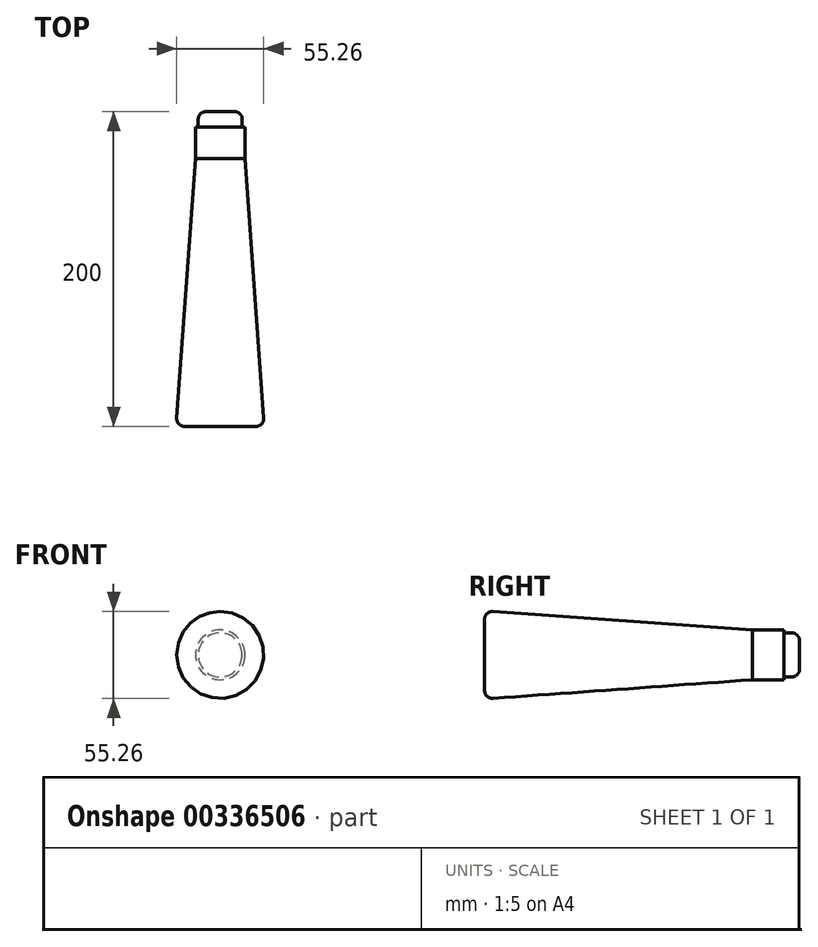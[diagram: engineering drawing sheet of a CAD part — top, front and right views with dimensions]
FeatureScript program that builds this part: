
annotation { "Feature Type Name" : "Feature", "Feature Type Description" : "" }
export const myFeature = defineFeature(function(context is Context, id is Id, definition is map)
    precondition{}
    {
        {
            var Q0;
            Q0=qCreatedBy(makeId("Top.planeOp"),FACE);
            var sketch = newSketch(context, id + "F0", { "sketchPlane" : qUnion([Q0])});
            skLineSegment(sketch, "E0", {"start": v(0, 0) * mm, "end": v(28, 0) * mm});
            skLineSegment(sketch, "E1", {"start": v(28, 0) * mm, "end": v(28, 170) * mm});
            skLineSegment(sketch, "E2", {"start": v(28, 170) * mm, "end": v(12.2, 170) * mm});
            skLineSegment(sketch, "E3", {"start": v(12.2, 170) * mm, "end": v(0, 0) * mm});
            skSolve(sketch);
        }
        {
            var Q0;
            Q0=makeQuery(id+"F0.imprint","IMPRINT",FACE,{"disambiguationData":[TD([[makeQuery(id+"F0.imprint","IMPRINT",EDGE,{"derivedFrom":sQuery(id+"F0.wireOp",EDGE,"E0")}),1.0]])]});
            var Q1;
            Q1=sQuery(id+"F0.wireOp",EDGE,"E1");
            revolve(context, id + "F1", {"entities" : qUnion([Q0]), "axis" : qUnion([Q1]), "revolveType" : RevolveType.FULL});
        }
        {
            var Q0;
            Q0=makeQuery(id+"F1.opRevolve","SWEPT_EDGE",EDGE,{"disambiguationData":[OSD([sQuery(id+"F0.wireOp",EDGE,"E0"),sQuery(id+"F0.wireOp",EDGE,"E3")])]});
            fillet(context, id + "F2", {"entities" : qUnion([Q0]), "radius" : 5 * mm, "tangentPropagation" : true, "allowEdgeOverflow" : false});
        }
        {
            var Q0;
            Q0=makeQuery(id+"F1.opRevolve","SWEPT_FACE",FACE,{"disambiguationData":[OSD([sQuery(id+"F0.wireOp",EDGE,"E2")])]});
            extrude(context, id + "F3", {"entities" : qUnion([Q0]), "depth" : 20 * mm});
        }
        {
            var Q0;
            Q0=makeQuery(id+"F3.opExtrude","CAP_FACE",FACE,{"disambiguationData":[OSD([sQuery(id+"F0.wireOp",EDGE,"E2")])],"isStart":false});
            var sketch = newSketch(context, id + "F4", { "sketchPlane" : qUnion([Q0])});
            skCircle(sketch, "E4", {"center": v(-28, 0) * mm, "radius": 14 * mm});
            skSolve(sketch);
        }
        {
            var Q0;
            Q0=makeQuery(id+"F4.imprint","IMPRINT",FACE,{"disambiguationData":[TD([[makeQuery(id+"F4.imprint","IMPRINT",EDGE,{"derivedFrom":sQuery(id+"F4.wireOp",EDGE,"E4")}),1.0]])]});
            extrude(context, id + "F5", {"entities" : qUnion([Q0]), "operationType" : NewBodyOperationType.ADD, "depth" : 10 * mm});
        }
        {
            var Q0;
            Q0=makeQuery(id+"F5.opExtrude","CAP_EDGE",EDGE,{"disambiguationData":[OSD([sQuery(id+"F4.wireOp",EDGE,"E4")])],"isStart":false});
            fillet(context, id + "F6", {"entities" : qUnion([Q0]), "radius" : 5 * mm, "tangentPropagation" : true, "allowEdgeOverflow" : false});
        }
    });
